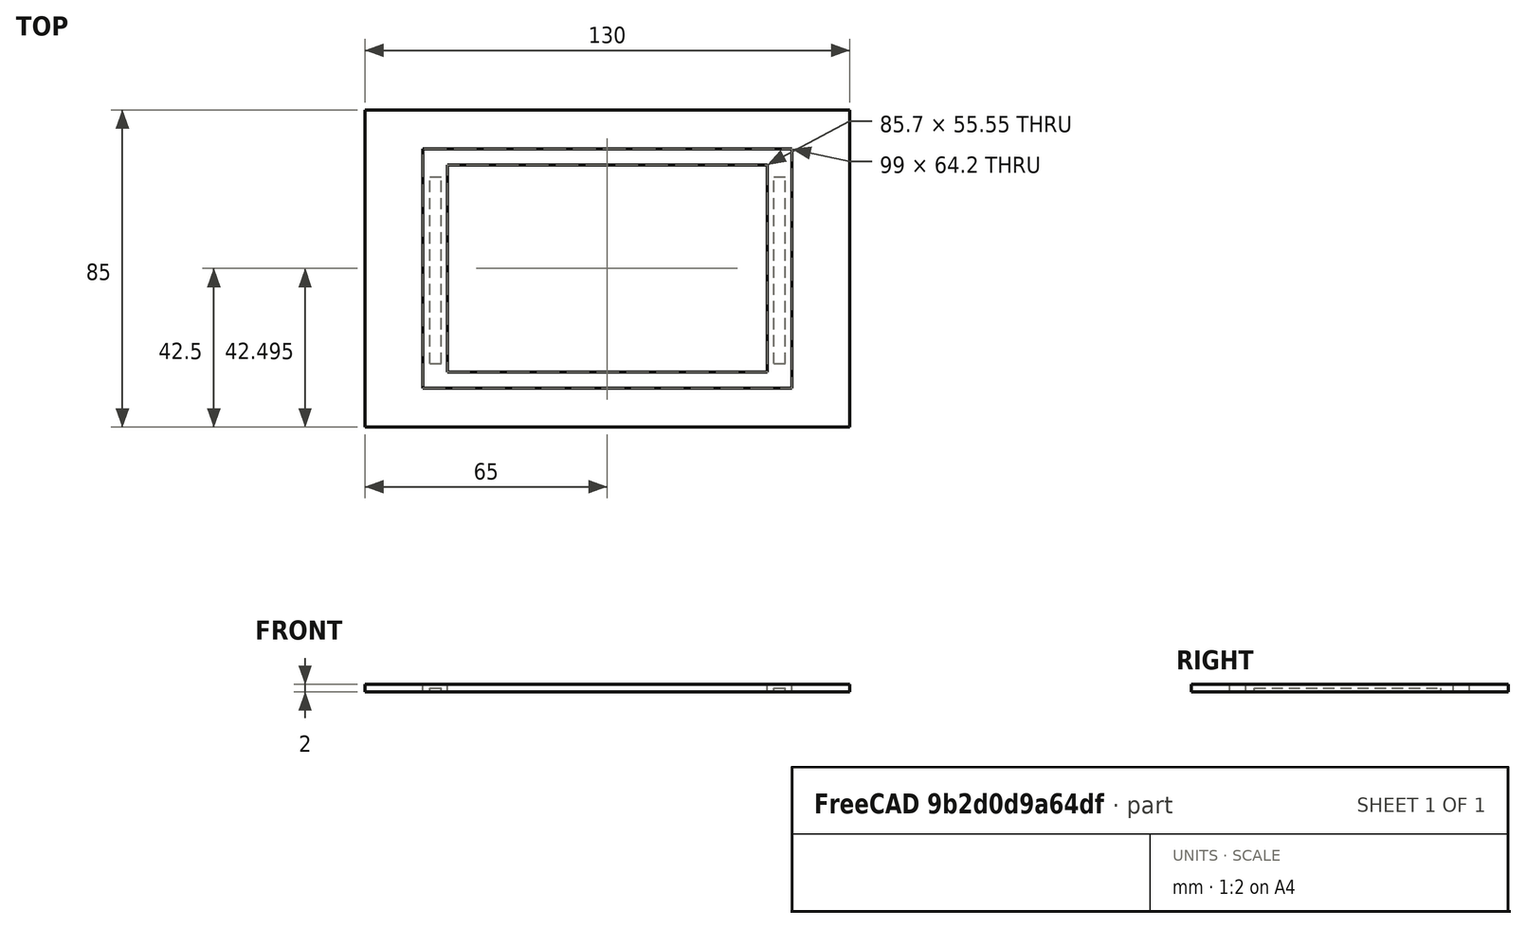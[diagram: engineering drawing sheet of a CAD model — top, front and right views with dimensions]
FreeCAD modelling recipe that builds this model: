
FCSTD DOCUMENT  (FreeCAD 0.16R)
Label: TFT
License: All rights reserved
LicenseURL: http://en.wikipedia.org/wiki/All_rights_reserved
objects: Part::Box×6, Part::Cut×4
note: 10 computed .brp shape members not serialized (recipe doc carries the construction recipe); baked Part::Feature solids carry a one-line shape summary decoded from their .brp

FEATURE [Part::Box] Box  label="Cube"
  Height = 2
  Length = 130
  Width = 85
FEATURE [Part::Box] Box001  label="Cube001"
  Height = 2
  Length = 99
  Placement = pos=(15.5,10.4,0) rot=(0,0,1;0rad)
  Width = 64.2
FEATURE [Part::Box] Box002  label="Cube002"
  Height = 2
  Length = 85.7
  Placement = pos=(22.15,14.72,0) rot=(0,0,1;0rad)
  Width = 55.55
FEATURE [Part::Cut] Cut
  Base = -> Box
  Tool = -> Box001
FEATURE [Part::Box] Box003  label="Cube003"
  Height = 2
  Length = 99
  Placement = pos=(15.5,10.4,0) rot=(0,0,1;0rad)
  Width = 64.2
FEATURE [Part::Cut] Cut001
  Base = -> Box003
  Tool = -> Box002
FEATURE [Part::Box] Box004  label="Cube004"
  Height = 1
  Length = 3
  Placement = pos=(17.5,17,0) rot=(0,0,1;0rad)
  Width = 50
FEATURE [Part::Box] Box005  label="Cube005"
  Height = 1
  Length = 3
  Placement = pos=(109.7,17,0) rot=(0,0,1;0rad)
  Width = 50
FEATURE [Part::Cut] Cut002
  Base = -> Cut001
  Tool = -> Box004
FEATURE [Part::Cut] Cut003
  Base = -> Cut002
  Tool = -> Box005
